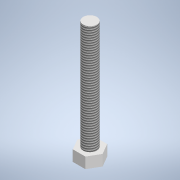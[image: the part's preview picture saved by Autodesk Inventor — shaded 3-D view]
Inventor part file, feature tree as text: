
AUTODESK INVENTOR PART (.ipt)
format: ipt  version: 2020 (Build 240168000, 168)  size: 112,640 bytes
history: native  units: mm
features: extrude x2, sketch x2, thread x1
ambient origin geometry x8: Origin, YZ Plane, XZ Plane, XY Plane, X Axis, Y Axis, Z Axis, Center Point
bodies: Solido1 (feature_tree)
feature tree (5):
  extrude  "Estrusione1"  Depth=5.0mm
  extrude  "Estrusione2"  Depth=40.0mm TaperAngle=0.0deg
  thread  "Filettatura1"
  sketch  "Schizzo1"
  sketch  "Schizzo2"
